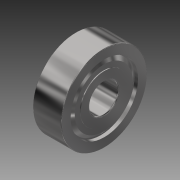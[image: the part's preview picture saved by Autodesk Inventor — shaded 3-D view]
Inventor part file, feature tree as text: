
AUTODESK INVENTOR PART (.ipt)
format: ipt  version: 2013 (Build 170138000, 138)  size: 647,680 bytes
history: native  units: in
note: dims shown in document units (in); Inventor stores cm internally (conversion verified against a paired STEP export)
features: other x11, imported_body x10, extrude x1, fillet x1, sketch x1
ambient origin geometry x8: Origin, YZ Plane, XZ Plane, XY Plane, X Axis, Y Axis, Z Axis, Center Point
feature tree (24):
  other  "1614ZZ"
  other  "1614ZZ1"
  extrude  "Extrusion1"  Depth=0.01in
  fillet  "Fillet1"  [1 undecoded]
  other  "1614ZZ_1"
  other  "1614ZZ_2"
  other  "1614ZZ_3"
  other  "1614ZZ_4"
  other  "1614ZZ_5"
  other  "1614ZZ_6"
  other  "1614ZZ_7"
  other  "1614ZZ_8"
  other  "1614ZZ_9"
  imported_body  "Base1"
  imported_body  "Base2"
  imported_body  "Base3"
  imported_body  "Base4"
  imported_body  "Base5"
  imported_body  "Base6"
  imported_body  "Base7"
  imported_body  "Base8"
  imported_body  "Base9"
  imported_body  "Base10"
  sketch  "Sketch1"  dims[d0=1.0in d1=0.0in d2=0.01in]
note: 1 required parameter value undecoded (feature->parameter linkage not recoverable at this tier; creation-order binding heuristic only, values carry confidence <= 0.55)
